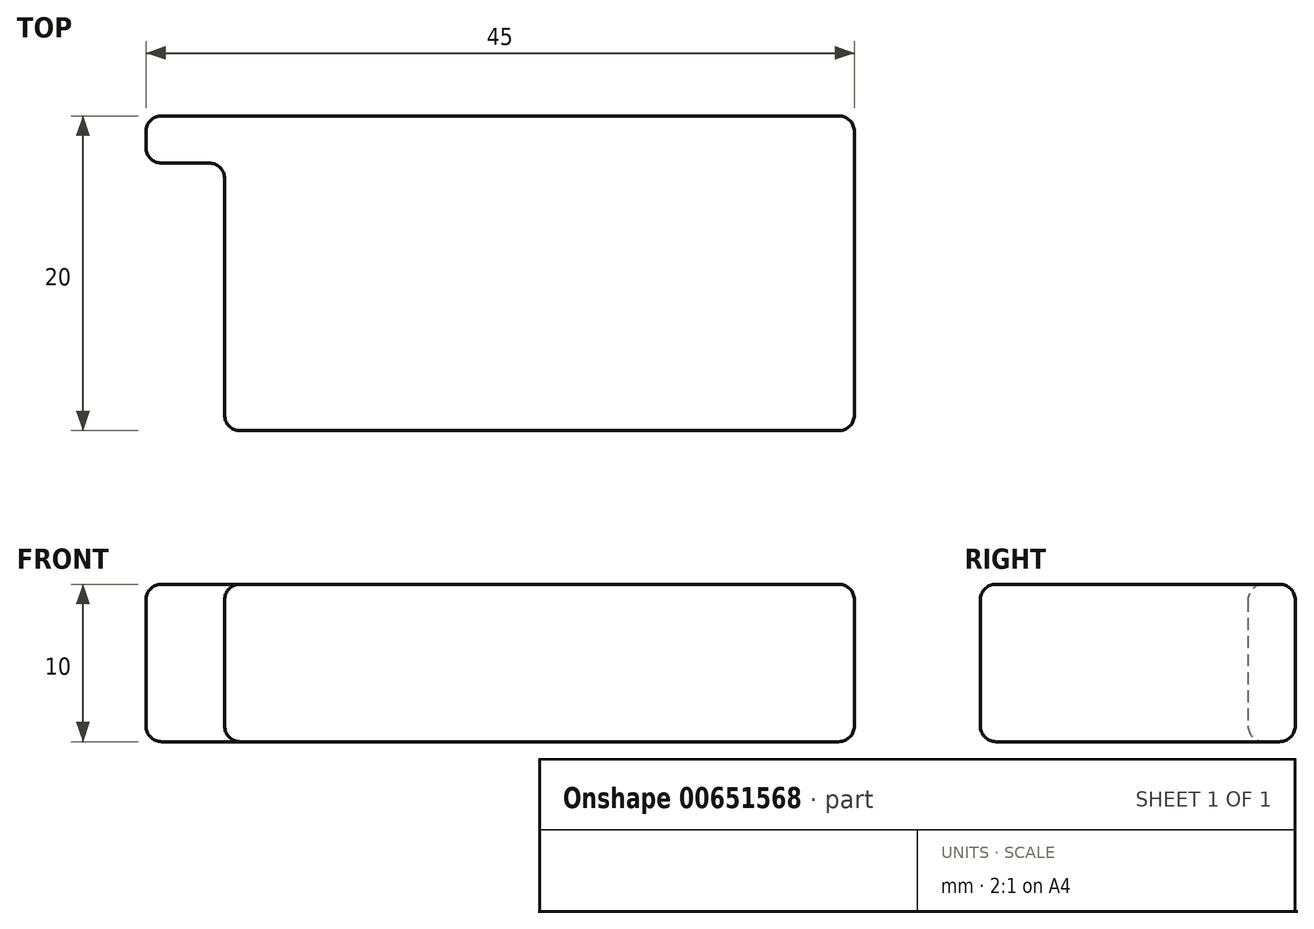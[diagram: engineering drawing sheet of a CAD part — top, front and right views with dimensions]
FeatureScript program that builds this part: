
annotation { "Feature Type Name" : "Feature", "Feature Type Description" : "" }
export const myFeature = defineFeature(function(context is Context, id is Id, definition is map)
    precondition{}
    {
        {
            var Q0;
            Q0=qCreatedBy(makeId("Top.planeOp"),FACE);
            var sketch = newSketch(context, id + "F0", { "sketchPlane" : qUnion([Q0])});
            skLineSegment(sketch, "E0", {"start": v(0, 0) * mm, "end": v(0, 20) * mm});
            skLineSegment(sketch, "E1", {"start": v(0, 20) * mm, "end": v(-45, 20) * mm});
            skLineSegment(sketch, "E2", {"start": v(-45, 20) * mm, "end": v(-45, 17) * mm});
            skLineSegment(sketch, "E3", {"start": v(-45, 17) * mm, "end": v(-40, 17) * mm});
            skLineSegment(sketch, "E4", {"start": v(-40, 17) * mm, "end": v(-40, 0) * mm});
            skLineSegment(sketch, "E5", {"start": v(-40, 0) * mm, "end": v(0, 0) * mm});
            skSolve(sketch);
        }
        {
            var Q0;
            Q0 = qSketchRegion(id + "F0", true);
            extrude(context, id + "F1", {"entities" : qUnion([Q0]), "depth" : 10 * mm, "offsetDistance" : 25 * mm});
        }
        {
            var Q0;
            Q0=makeQuery(id+"F1.opExtrude","SWEPT_EDGE",EDGE,{"disambiguationData":[OSD([sQuery(id+"F0.wireOp",EDGE,"E1"),sQuery(id+"F0.wireOp",EDGE,"E2")])]});
            var Q1;
            Q1=makeQuery(id+"F1.opExtrude","SWEPT_FACE",FACE,{"disambiguationData":[OSD([sQuery(id+"F0.wireOp",EDGE,"E0")])]});
            var Q2;
            Q2=makeQuery(id+"F1.opExtrude","CAP_FACE",FACE,{"disambiguationData":[OSD([sQuery(id+"F0.wireOp",EDGE,"E0"),sQuery(id+"F0.wireOp",EDGE,"E1"),sQuery(id+"F0.wireOp",EDGE,"E2"),sQuery(id+"F0.wireOp",EDGE,"E3"),sQuery(id+"F0.wireOp",EDGE,"E4"),sQuery(id+"F0.wireOp",EDGE,"E5")])],"isStart":true});
            var Q3;
            Q3=makeQuery(id+"F1.opExtrude","SWEPT_FACE",FACE,{"disambiguationData":[OSD([sQuery(id+"F0.wireOp",EDGE,"E2")])]});
            var Q4;
            Q4=makeQuery(id+"F1.opExtrude","CAP_FACE",FACE,{"disambiguationData":[OSD([sQuery(id+"F0.wireOp",EDGE,"E0"),sQuery(id+"F0.wireOp",EDGE,"E1"),sQuery(id+"F0.wireOp",EDGE,"E2"),sQuery(id+"F0.wireOp",EDGE,"E3"),sQuery(id+"F0.wireOp",EDGE,"E4"),sQuery(id+"F0.wireOp",EDGE,"E5")])],"isStart":false});
            var Q5;
            Q5=makeQuery(id+"F1.opExtrude","SWEPT_EDGE",EDGE,{"disambiguationData":[OSD([sQuery(id+"F0.wireOp",EDGE,"E0"),sQuery(id+"F0.wireOp",EDGE,"E1")])]});
            var Q6;
            Q6=makeQuery(id+"F1.opExtrude","CAP_EDGE",EDGE,{"disambiguationData":[OSD([sQuery(id+"F0.wireOp",EDGE,"E4")])],"isStart":false});
            var Q7;
            Q7=makeQuery(id+"F1.opExtrude","SWEPT_EDGE",EDGE,{"disambiguationData":[OSD([sQuery(id+"F0.wireOp",EDGE,"E2"),sQuery(id+"F0.wireOp",EDGE,"E3")])]});
            var Q8;
            Q8=makeQuery(id+"F1.opExtrude","SWEPT_FACE",FACE,{"disambiguationData":[OSD([sQuery(id+"F0.wireOp",EDGE,"E1")])]});
            var Q9;
            Q9=makeQuery(id+"F1.opExtrude","CAP_EDGE",EDGE,{"disambiguationData":[OSD([sQuery(id+"F0.wireOp",EDGE,"E4")])],"isStart":true});
            var Q10;
            Q10=makeQuery(id+"F1.opExtrude","SWEPT_EDGE",EDGE,{"disambiguationData":[OSD([sQuery(id+"F0.wireOp",EDGE,"E4"),sQuery(id+"F0.wireOp",EDGE,"E5")])]});
            var Q11;
            Q11=makeQuery(id+"F1.opExtrude","SWEPT_FACE",FACE,{"disambiguationData":[OSD([sQuery(id+"F0.wireOp",EDGE,"E4")])]});
            var Q12;
            Q12=makeQuery(id+"F1.opExtrude","CAP_EDGE",EDGE,{"disambiguationData":[OSD([sQuery(id+"F0.wireOp",EDGE,"E0")])],"isStart":false});
            var Q13;
            Q13=makeQuery(id+"F1.opExtrude","SWEPT_FACE",FACE,{"disambiguationData":[OSD([sQuery(id+"F0.wireOp",EDGE,"E5")])]});
            var Q14;
            Q14=makeQuery(id+"F1.opExtrude","CAP_EDGE",EDGE,{"disambiguationData":[OSD([sQuery(id+"F0.wireOp",EDGE,"E1")])],"isStart":true});
            var Q15;
            Q15=makeQuery(id+"F1.opExtrude","CAP_EDGE",EDGE,{"disambiguationData":[OSD([sQuery(id+"F0.wireOp",EDGE,"E1")])],"isStart":false});
            var Q16;
            Q16=makeQuery(id+"F1.opExtrude","SWEPT_EDGE",EDGE,{"disambiguationData":[OSD([sQuery(id+"F0.wireOp",EDGE,"E3"),sQuery(id+"F0.wireOp",EDGE,"E4")])]});
            var Q17;
            Q17=makeQuery(id+"F1.opExtrude","SWEPT_EDGE",EDGE,{"disambiguationData":[OSD([sQuery(id+"F0.wireOp",EDGE,"E0"),sQuery(id+"F0.wireOp",EDGE,"E5")])]});
            var Q18;
            Q18=makeQuery(id+"F1.opExtrude","CAP_EDGE",EDGE,{"disambiguationData":[OSD([sQuery(id+"F0.wireOp",EDGE,"E3")])],"isStart":false});
            var Q19;
            Q19=makeQuery(id+"F1.opExtrude","SWEPT_FACE",FACE,{"disambiguationData":[OSD([sQuery(id+"F0.wireOp",EDGE,"E3")])]});
            var Q20;
            Q20=makeQuery(id+"F1.opExtrude","CAP_EDGE",EDGE,{"disambiguationData":[OSD([sQuery(id+"F0.wireOp",EDGE,"E0")])],"isStart":true});
            var Q21;
            Q21=makeQuery(id+"F1.opExtrude","CAP_EDGE",EDGE,{"disambiguationData":[OSD([sQuery(id+"F0.wireOp",EDGE,"E2")])],"isStart":true});
            var Q22;
            Q22=makeQuery(id+"F1.opExtrude","CAP_EDGE",EDGE,{"disambiguationData":[OSD([sQuery(id+"F0.wireOp",EDGE,"E2")])],"isStart":false});
            var Q23;
            Q23=makeQuery(id+"F1.opExtrude","CAP_EDGE",EDGE,{"disambiguationData":[OSD([sQuery(id+"F0.wireOp",EDGE,"E5")])],"isStart":true});
            var Q24;
            Q24=makeQuery(id+"F1.opExtrude","CAP_EDGE",EDGE,{"disambiguationData":[OSD([sQuery(id+"F0.wireOp",EDGE,"E5")])],"isStart":false});
            var Q25;
            Q25=makeQuery(id+"F1.opExtrude","CAP_EDGE",EDGE,{"disambiguationData":[OSD([sQuery(id+"F0.wireOp",EDGE,"E3")])],"isStart":true});
            fillet(context, id + "F2", {"entities" : qUnion([Q0, Q1, Q2, Q3, Q4, Q5, Q6, Q7, Q8, Q9, Q10, Q11, Q12, Q13, Q14, Q15, Q16, Q17, Q18, Q19, Q20, Q21, Q22, Q23, Q24, Q25]), "radius" : 1 * mm, "tangentPropagation" : true, "allowEdgeOverflow" : false});
        }
    });
